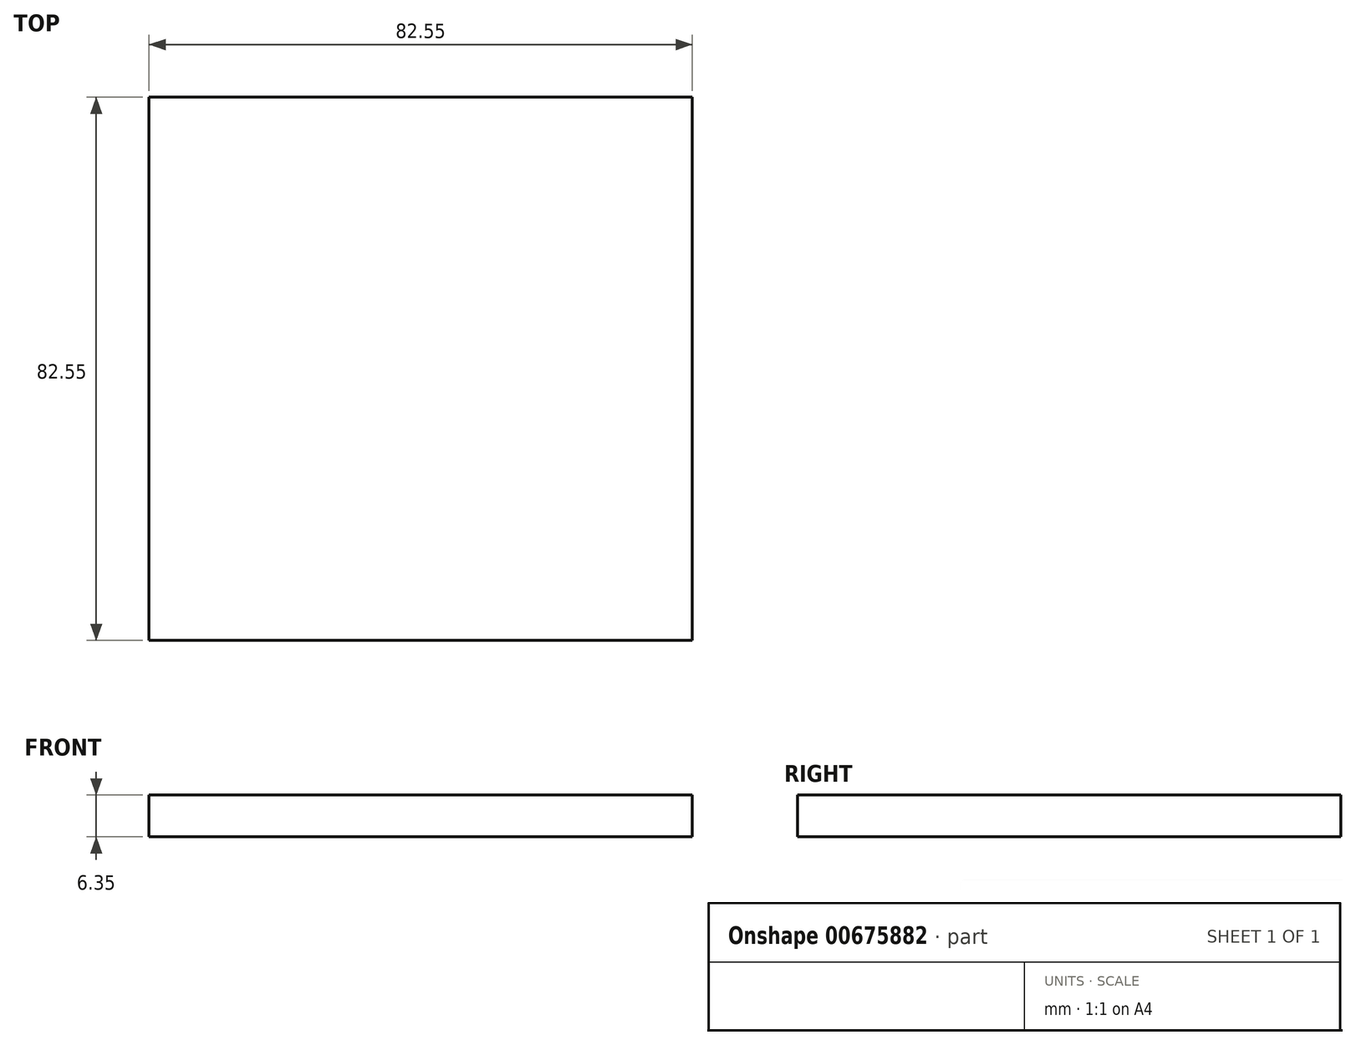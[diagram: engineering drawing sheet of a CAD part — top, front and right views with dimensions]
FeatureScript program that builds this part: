
annotation { "Feature Type Name" : "Feature", "Feature Type Description" : "" }
export const myFeature = defineFeature(function(context is Context, id is Id, definition is map)
    precondition{}
    {
        {
            var Q0;
            Q0=qCreatedBy(makeId("Top.planeOp"),FACE);
            var sketch = newSketch(context, id + "F0", { "sketchPlane" : qUnion([Q0])});
            skLineSegment(sketch, "E0.bottom", {"start": v(0, 0) * mm, "end": v(82.55, 0) * mm});
            skLineSegment(sketch, "E0.top", {"start": v(0, -82.55) * mm, "end": v(82.55, -82.55) * mm});
            skLineSegment(sketch, "E0.left", {"start": v(0, 0) * mm, "end": v(0, -82.55) * mm});
            skLineSegment(sketch, "E0.right", {"start": v(82.55, 0) * mm, "end": v(82.55, -82.55) * mm});
            skSolve(sketch);
        }
        {
            var Q0;
            Q0=makeQuery(id+"F0.imprint","IMPRINT",FACE,{"disambiguationData":[TD([[makeQuery(id+"F0.imprint","IMPRINT",EDGE,{"derivedFrom":sQuery(id+"F0.wireOp",EDGE,"E0.bottom")}),-1.0]])]});
            extrude(context, id + "F1", {"entities" : qUnion([Q0]), "depth" : 6.35 * mm, "offsetDistance" : 25.4 * mm});
        }
    });
